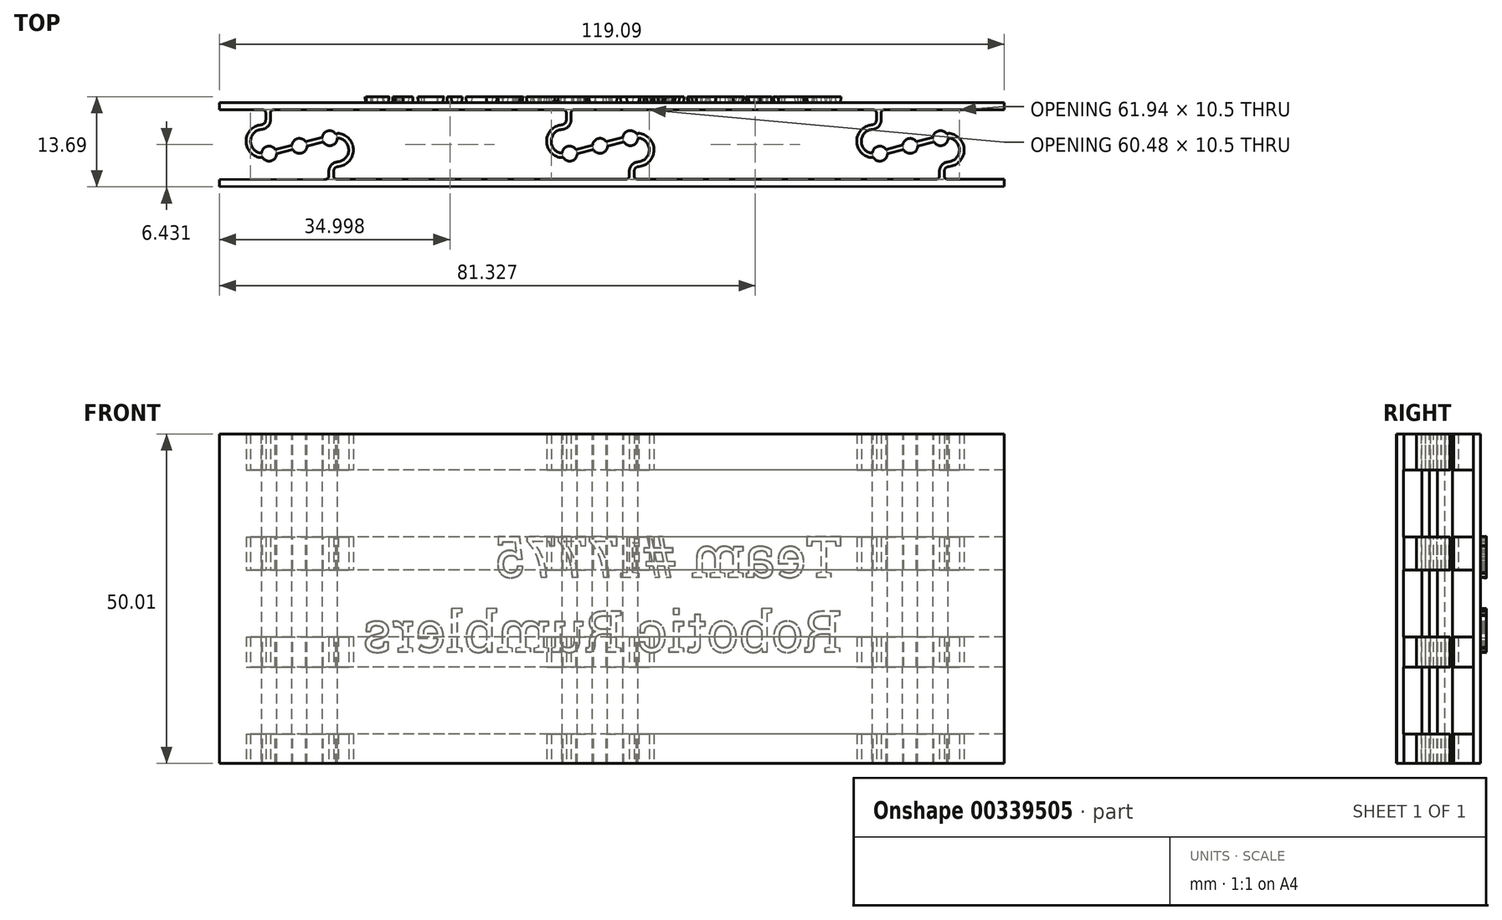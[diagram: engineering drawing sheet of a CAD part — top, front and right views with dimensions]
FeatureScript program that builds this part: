
annotation { "Feature Type Name" : "Feature", "Feature Type Description" : "" }
export const myFeature = defineFeature(function(context is Context, id is Id, definition is map)
    precondition{}
    {
        {
            var Q0;
            Q0=qCreatedBy(makeId("Top.planeOp"),FACE);
            var sketch = newSketch(context, id + "F0", { "sketchPlane" : qUnion([Q0])});
            skLineSegment(sketch, "E0", {"start": v(159.96, 0.09) * mm, "end": v(159.96, -1.43) * mm});
            skLineSegment(sketch, "E1", {"start": v(160.97, 0.09) * mm, "end": v(160.97, -1.43) * mm});
            skArc(sketch, "E2", {"start": v(160.97, -1.43) * mm, "mid": v(160.38, -2.87) * mm, "end": v(158.93, -3.46) * mm});
            skArc(sketch, "E3", {"start": v(159.96, -1.43) * mm, "mid": v(159.67, -2.16) * mm, "end": v(158.95, -2.48) * mm});
            skArc(sketch, "E4", {"start": v(158.93, -3.46) * mm, "mid": v(156.76, -5.9) * mm, "end": v(158.8, -8.45) * mm});
            skArc(sketch, "E5", {"start": v(158.95, -2.48) * mm, "mid": v(155.8, -5.9) * mm, "end": v(158.81, -9.43) * mm});
            skLineSegment(sketch, "E6", {"start": v(174.33, -13.38) * mm, "end": v(174.33, -12.37) * mm});
            skLineSegment(sketch, "E7", {"start": v(173.31, -13.38) * mm, "end": v(173.31, -12.37) * mm});
            skArc(sketch, "E8", {"start": v(173.31, -12.37) * mm, "mid": v(173.9, -10.94) * mm, "end": v(175.3, -10.32) * mm});
            skArc(sketch, "E9", {"start": v(174.33, -12.37) * mm, "mid": v(174.63, -11.63) * mm, "end": v(175.37, -11.32) * mm});
            skArc(sketch, "E10", {"start": v(175.3, -10.32) * mm, "mid": v(177.55, -7.87) * mm, "end": v(175.43, -5.3) * mm});
            skArc(sketch, "E11", {"start": v(175.37, -11.32) * mm, "mid": v(178.55, -7.83) * mm, "end": v(175.4, -4.29) * mm});
            skLineSegment(sketch, "E12", {"start": v(159.04, -9.42) * mm, "end": v(175.18, -5.32) * mm});
            skLineSegment(sketch, "E13", {"start": v(175.2, -4.3) * mm, "end": v(159.06, -8.44) * mm});
            skPoint(sketch, "E14.visualSharp", {"position": v(158.93, -8.47) * mm});
            skArc(sketch, "E14.filletArc", {"start": v(158.8, -8.45) * mm, "mid": v(158.92, -8.46) * mm, "end": v(159.06, -8.44) * mm});
            skPoint(sketch, "E15.visualSharp", {"position": v(158.93, -9.45) * mm});
            skArc(sketch, "E15.filletArc", {"start": v(158.81, -9.43) * mm, "mid": v(158.93, -9.44) * mm, "end": v(159.04, -9.42) * mm});
            skPoint(sketch, "E16.visualSharp", {"position": v(175.3, -4.28) * mm});
            skArc(sketch, "E16.filletArc", {"start": v(175.4, -4.29) * mm, "mid": v(175.3, -4.29) * mm, "end": v(175.2, -4.3) * mm});
            skPoint(sketch, "E17.visualSharp", {"position": v(175.3, -5.29) * mm});
            skArc(sketch, "E17.filletArc", {"start": v(175.43, -5.3) * mm, "mid": v(175.3, -5.3) * mm, "end": v(175.18, -5.32) * mm});
            skLineSegment(sketch, "E18", {"start": v(44.92, -13.98) * mm, "end": v(172.72, -13.98) * mm});
            skLineSegment(sketch, "E19", {"start": v(161.57, 0.68) * mm, "end": v(187.04, 0.68) * mm});
            skLineSegment(sketch, "E20", {"start": v(187.04, 0.68) * mm, "end": v(187.04, 2.22) * mm});
            skLineSegment(sketch, "E21", {"start": v(174.93, -13.98) * mm, "end": v(187.04, -13.98) * mm});
            skLineSegment(sketch, "E22", {"start": v(187.04, -13.98) * mm, "end": v(187.04, -15.5) * mm});
            skPoint(sketch, "E23.visualSharp", {"position": v(160.97, 0.68) * mm});
            skArc(sketch, "E23.filletArc", {"start": v(161.57, 0.68) * mm, "mid": v(161.15, 0.5) * mm, "end": v(160.97, 0.09) * mm});
            skPoint(sketch, "E24.visualSharp", {"position": v(159.96, 0.68) * mm});
            skArc(sketch, "E24.filletArc", {"start": v(159.96, 0.09) * mm, "mid": v(159.78, 0.5) * mm, "end": v(159.36, 0.68) * mm});
            skPoint(sketch, "E25.visualSharp", {"position": v(174.33, -13.98) * mm});
            skArc(sketch, "E25.filletArc", {"start": v(174.33, -13.38) * mm, "mid": v(174.5, -13.8) * mm, "end": v(174.93, -13.98) * mm});
            skPoint(sketch, "E26.visualSharp", {"position": v(173.31, -13.98) * mm});
            skArc(sketch, "E26.filletArc", {"start": v(172.72, -13.98) * mm, "mid": v(173.14, -13.8) * mm, "end": v(173.31, -13.38) * mm});
            skLineSegment(sketch, "E27", {"start": v(31.57, 0.09) * mm, "end": v(31.57, -1.43) * mm});
            skArc(sketch, "E28", {"start": v(31.57, -1.43) * mm, "mid": v(30.97, -2.87) * mm, "end": v(29.52, -3.46) * mm});
            skArc(sketch, "E29", {"start": v(30.55, -1.43) * mm, "mid": v(30.26, -2.16) * mm, "end": v(29.54, -2.48) * mm});
            skArc(sketch, "E30", {"start": v(29.52, -3.46) * mm, "mid": v(27.35, -5.9) * mm, "end": v(29.38, -8.45) * mm});
            skArc(sketch, "E31", {"start": v(29.54, -2.48) * mm, "mid": v(26.38, -5.9) * mm, "end": v(29.4, -9.43) * mm});
            skLineSegment(sketch, "E32", {"start": v(44.92, -13.38) * mm, "end": v(44.92, -12.37) * mm});
            skLineSegment(sketch, "E33", {"start": v(43.9, -13.38) * mm, "end": v(43.9, -12.37) * mm});
            skArc(sketch, "E34", {"start": v(43.9, -12.37) * mm, "mid": v(44.48, -10.94) * mm, "end": v(45.89, -10.32) * mm});
            skArc(sketch, "E35", {"start": v(44.92, -12.37) * mm, "mid": v(45.22, -11.63) * mm, "end": v(45.96, -11.32) * mm});
            skArc(sketch, "E36", {"start": v(45.89, -10.32) * mm, "mid": v(48.14, -7.87) * mm, "end": v(46.02, -5.3) * mm});
            skArc(sketch, "E37", {"start": v(45.96, -11.32) * mm, "mid": v(49.14, -7.83) * mm, "end": v(46, -4.29) * mm});
            skLineSegment(sketch, "E38", {"start": v(29.63, -9.42) * mm, "end": v(45.77, -5.32) * mm});
            skLineSegment(sketch, "E39", {"start": v(45.78, -4.3) * mm, "end": v(29.65, -8.44) * mm});
            skPoint(sketch, "E40.visualSharp", {"position": v(29.52, -8.47) * mm});
            skArc(sketch, "E40.filletArc", {"start": v(29.38, -8.45) * mm, "mid": v(29.52, -8.46) * mm, "end": v(29.65, -8.44) * mm});
            skPoint(sketch, "E41.visualSharp", {"position": v(29.52, -9.45) * mm});
            skArc(sketch, "E41.filletArc", {"start": v(29.4, -9.43) * mm, "mid": v(29.52, -9.44) * mm, "end": v(29.63, -9.42) * mm});
            skPoint(sketch, "E42.visualSharp", {"position": v(45.89, -4.28) * mm});
            skArc(sketch, "E42.filletArc", {"start": v(46, -4.29) * mm, "mid": v(45.9, -4.29) * mm, "end": v(45.78, -4.3) * mm});
            skPoint(sketch, "E43.visualSharp", {"position": v(45.89, -5.29) * mm});
            skArc(sketch, "E43.filletArc", {"start": v(46.02, -5.3) * mm, "mid": v(45.9, -5.3) * mm, "end": v(45.77, -5.32) * mm});
            skPoint(sketch, "E44.visualSharp", {"position": v(31.57, 0) * mm});
            skArc(sketch, "E44.filletArc", {"start": v(32.16, 0.68) * mm, "mid": v(31.74, 0.5) * mm, "end": v(31.57, 0.09) * mm});
            skPoint(sketch, "E45.visualSharp", {"position": v(44.92, -13.98) * mm});
            skArc(sketch, "E45.filletArc", {"start": v(44.92, -13.38) * mm, "mid": v(45.1, -13.8) * mm, "end": v(45.52, -13.98) * mm});
            skPoint(sketch, "E46.visualSharp", {"position": v(43.9, -13.98) * mm});
            skArc(sketch, "E46.filletArc", {"start": v(43.31, -13.98) * mm, "mid": v(43.73, -13.8) * mm, "end": v(43.9, -13.38) * mm});
            skLineSegment(sketch, "E47", {"start": v(187.04, 2.22) * mm, "end": v(20.7, 2.22) * mm});
            skLineSegment(sketch, "E48", {"start": v(43.31, -13.98) * mm, "end": v(20.7, -14.1) * mm});
            skLineSegment(sketch, "E49", {"start": v(20.7, -14.1) * mm, "end": v(20.71, -15.63) * mm});
            skLineSegment(sketch, "E50", {"start": v(20.71, -15.63) * mm, "end": v(187.04, -15.5) * mm});
            skLineSegment(sketch, "E51", {"start": v(20.7, 2.22) * mm, "end": v(20.7, 0.7) * mm});
            skLineSegment(sketch, "E52", {"start": v(30.55, -1.43) * mm, "end": v(30.55, 0.1) * mm});
            skLineSegment(sketch, "E53", {"start": v(29.95, 0.7) * mm, "end": v(20.7, 0.7) * mm});
            skPoint(sketch, "E54.visualSharp", {"position": v(30.55, 0.7) * mm});
            skArc(sketch, "E54.filletArc", {"start": v(30.55, 0.1) * mm, "mid": v(30.38, 0.52) * mm, "end": v(29.95, 0.7) * mm});
            skLineSegment(sketch, "E55", {"start": v(94.24, 0.09) * mm, "end": v(94.24, -1.43) * mm});
            skLineSegment(sketch, "E56", {"start": v(95.25, 0.09) * mm, "end": v(95.25, -1.43) * mm});
            skArc(sketch, "E57", {"start": v(95.25, -1.43) * mm, "mid": v(94.66, -2.87) * mm, "end": v(93.21, -3.46) * mm});
            skArc(sketch, "E58", {"start": v(94.24, -1.43) * mm, "mid": v(93.94, -2.16) * mm, "end": v(93.23, -2.48) * mm});
            skArc(sketch, "E59", {"start": v(93.21, -3.46) * mm, "mid": v(91.04, -5.9) * mm, "end": v(93.07, -8.45) * mm});
            skArc(sketch, "E60", {"start": v(93.23, -2.48) * mm, "mid": v(90.07, -5.9) * mm, "end": v(93.1, -9.43) * mm});
            skLineSegment(sketch, "E61", {"start": v(108.61, -13.38) * mm, "end": v(108.61, -12.37) * mm});
            skLineSegment(sketch, "E62", {"start": v(107.6, -13.38) * mm, "end": v(107.6, -12.37) * mm});
            skArc(sketch, "E63", {"start": v(107.6, -12.37) * mm, "mid": v(108.17, -10.94) * mm, "end": v(109.57, -10.32) * mm});
            skArc(sketch, "E64", {"start": v(108.61, -12.37) * mm, "mid": v(108.91, -11.63) * mm, "end": v(109.64, -11.32) * mm});
            skArc(sketch, "E65", {"start": v(109.57, -10.32) * mm, "mid": v(111.83, -7.87) * mm, "end": v(109.7, -5.3) * mm});
            skArc(sketch, "E66", {"start": v(109.64, -11.32) * mm, "mid": v(112.83, -7.83) * mm, "end": v(109.69, -4.29) * mm});
            skLineSegment(sketch, "E67", {"start": v(93.32, -9.42) * mm, "end": v(109.46, -5.32) * mm});
            skLineSegment(sketch, "E68", {"start": v(109.47, -4.3) * mm, "end": v(93.34, -8.44) * mm});
            skPoint(sketch, "E69.visualSharp", {"position": v(93.21, -8.47) * mm});
            skArc(sketch, "E69.filletArc", {"start": v(93.07, -8.45) * mm, "mid": v(93.2, -8.46) * mm, "end": v(93.34, -8.44) * mm});
            skPoint(sketch, "E70.visualSharp", {"position": v(93.21, -9.45) * mm});
            skArc(sketch, "E70.filletArc", {"start": v(93.1, -9.43) * mm, "mid": v(93.2, -9.44) * mm, "end": v(93.32, -9.42) * mm});
            skPoint(sketch, "E71.visualSharp", {"position": v(109.57, -4.28) * mm});
            skArc(sketch, "E71.filletArc", {"start": v(109.69, -4.29) * mm, "mid": v(109.58, -4.29) * mm, "end": v(109.47, -4.3) * mm});
            skPoint(sketch, "E72.visualSharp", {"position": v(109.57, -5.29) * mm});
            skArc(sketch, "E72.filletArc", {"start": v(109.7, -5.3) * mm, "mid": v(109.58, -5.3) * mm, "end": v(109.46, -5.32) * mm});
            skPoint(sketch, "E73.visualSharp", {"position": v(95.25, 0.68) * mm});
            skArc(sketch, "E73.filletArc", {"start": v(95.85, 0.68) * mm, "mid": v(95.43, 0.5) * mm, "end": v(95.25, 0.09) * mm});
            skPoint(sketch, "E74.visualSharp", {"position": v(94.24, 0.68) * mm});
            skArc(sketch, "E74.filletArc", {"start": v(94.24, 0.09) * mm, "mid": v(94.06, 0.5) * mm, "end": v(93.64, 0.68) * mm});
            skPoint(sketch, "E75.visualSharp", {"position": v(108.61, -13.98) * mm});
            skArc(sketch, "E75.filletArc", {"start": v(108.61, -13.38) * mm, "mid": v(108.79, -13.8) * mm, "end": v(109.2, -13.98) * mm});
            skPoint(sketch, "E76.visualSharp", {"position": v(107.6, -13.98) * mm});
            skArc(sketch, "E76.filletArc", {"start": v(107, -13.98) * mm, "mid": v(107.42, -13.8) * mm, "end": v(107.6, -13.38) * mm});
            skLineSegment(sketch, "E77", {"start": v(32.16, 0.68) * mm, "end": v(93.64, 0.68) * mm});
            skLineSegment(sketch, "E78", {"start": v(95.85, 0.68) * mm, "end": v(159.36, 0.68) * mm});
            skSolve(sketch);
        }
        {
            var Q0;
            Q0=makeQuery(id+"F0.imprint","IMPRINT",FACE,{"disambiguationData":[TD([[makeQuery(id+"F0.imprint","IMPRINT",EDGE,{"derivedFrom":sQuery(id+"F0.wireOp",EDGE,"E0")}),1.0]])]});
            extrude(context, id + "F1", {"entities" : qUnion([Q0]), "depth" : 69.85 * mm});
        }
        {
            var Q0;
            Q0=makeQuery(id+"F1.opExtrude","SWEPT_FACE",FACE,{"disambiguationData":[OSD([sQuery(id+"F0.wireOp",EDGE,"E51")])]});
            var sketch = newSketch(context, id + "F2", { "sketchPlane" : qUnion([Q0])});
            skLineSegment(sketch, "E79.bottom", {"start": v(-0.7, 6.25) * mm, "end": v(14.06, 6.25) * mm});
            skLineSegment(sketch, "E79.top", {"start": v(-0.7, 20.44) * mm, "end": v(14.06, 20.44) * mm});
            skLineSegment(sketch, "E79.left", {"start": v(-0.7, 6.25) * mm, "end": v(-0.7, 20.44) * mm});
            skLineSegment(sketch, "E79.right", {"start": v(14.06, 6.25) * mm, "end": v(14.06, 20.44) * mm});
            skLineSegment(sketch, "E80.bottom", {"start": v(-0.7, 26.84) * mm, "end": v(14.06, 26.84) * mm});
            skLineSegment(sketch, "E80.top", {"start": v(-0.7, 41.03) * mm, "end": v(14.06, 41.03) * mm});
            skLineSegment(sketch, "E80.left", {"start": v(-0.7, 26.84) * mm, "end": v(-0.7, 41.03) * mm});
            skLineSegment(sketch, "E80.right", {"start": v(14.06, 26.84) * mm, "end": v(14.06, 41.03) * mm});
            skLineSegment(sketch, "E81.bottom", {"start": v(-0.7, 48.02) * mm, "end": v(14.06, 48.02) * mm});
            skLineSegment(sketch, "E81.top", {"start": v(-0.7, 62.2) * mm, "end": v(14.06, 62.2) * mm});
            skLineSegment(sketch, "E81.left", {"start": v(-0.7, 48.02) * mm, "end": v(-0.7, 62.2) * mm});
            skLineSegment(sketch, "E81.right", {"start": v(14.06, 48.02) * mm, "end": v(14.06, 62.2) * mm});
            skSolve(sketch);
        }
        {
            var Q0;
            Q0=makeQuery(id+"F2.imprint","IMPRINT",FACE,{"disambiguationData":[TD([[makeQuery(id+"F2.imprint","IMPRINT",EDGE,{"derivedFrom":sQuery(id+"F2.wireOp",EDGE,"E79.bottom")}),1.0]])]});
            var Q1;
            Q1=makeQuery(id+"F2.imprint","IMPRINT",FACE,{"disambiguationData":[TD([[makeQuery(id+"F2.imprint","IMPRINT",EDGE,{"derivedFrom":sQuery(id+"F2.wireOp",EDGE,"E80.bottom")}),1.0]])]});
            var Q2;
            Q2=makeQuery(id+"F2.imprint","IMPRINT",FACE,{"disambiguationData":[TD([[makeQuery(id+"F2.imprint","IMPRINT",EDGE,{"derivedFrom":sQuery(id+"F2.wireOp",EDGE,"E81.bottom")}),1.0]])]});
            extrude(context, id + "F3", {"entities" : qUnion([Q0, Q1, Q2]), "operationType" : NewBodyOperationType.REMOVE, "oppositeDirection" : true, "depth" : 254 * mm});
        }
        {
            var Q0;
            Q0=makeQuery(id+"F1.opExtrude","SWEPT_FACE",FACE,{"disambiguationData":[OSD([sQuery(id+"F0.wireOp",EDGE,"E47")])]});
            var sketch = newSketch(context, id + "F4", { "sketchPlane" : qUnion([Q0])});
            skText(sketch, "E82", { "text": "Team #17775\nRobotic Rumblers", "fontName": "RobotoSlab-Regular.ttf"});
            const initialGuessF4  = {"E82": [-0.15258, 0.03953, 1, 0, 0.00865]};
            skSetInitialGuess(sketch, initialGuessF4);
            skSolve(sketch);
        }
        {
            var Q0;
            Q0=qSketchRegion(id+"F4",true);
            extrude(context, id + "F5", {"entities" : qUnion([Q0]), "operationType" : NewBodyOperationType.ADD, "depth" : 1.27 * mm, "hasDraft" : true, "draftAngle" : 3 * degree});
        }
        {
            var Q0;
            Q0=makeQuery(id+"F1.opExtrude","SWEPT_BODY",BODY,{"disambiguationData":[OSD([sQuery(id+"F0.wireOp",EDGE,"E0"),sQuery(id+"F0.wireOp",EDGE,"E1"),sQuery(id+"F0.wireOp",EDGE,"E2"),sQuery(id+"F0.wireOp",EDGE,"E3"),sQuery(id+"F0.wireOp",EDGE,"E4"),sQuery(id+"F0.wireOp",EDGE,"E5"),sQuery(id+"F0.wireOp",EDGE,"E6"),sQuery(id+"F0.wireOp",EDGE,"E7"),sQuery(id+"F0.wireOp",EDGE,"E8"),sQuery(id+"F0.wireOp",EDGE,"E9"),sQuery(id+"F0.wireOp",EDGE,"E10"),sQuery(id+"F0.wireOp",EDGE,"E11"),sQuery(id+"F0.wireOp",EDGE,"E12"),sQuery(id+"F0.wireOp",EDGE,"E13"),sQuery(id+"F0.wireOp",EDGE,"E14.filletArc"),sQuery(id+"F0.wireOp",EDGE,"E15.filletArc"),sQuery(id+"F0.wireOp",EDGE,"E16.filletArc"),sQuery(id+"F0.wireOp",EDGE,"E17.filletArc"),sQuery(id+"F0.wireOp",EDGE,"E18"),sQuery(id+"F0.wireOp",EDGE,"E19"),sQuery(id+"F0.wireOp",EDGE,"E20"),sQuery(id+"F0.wireOp",EDGE,"E21"),sQuery(id+"F0.wireOp",EDGE,"E22"),sQuery(id+"F0.wireOp",EDGE,"E23.filletArc"),sQuery(id+"F0.wireOp",EDGE,"E24.filletArc"),sQuery(id+"F0.wireOp",EDGE,"E25.filletArc"),sQuery(id+"F0.wireOp",EDGE,"E26.filletArc"),sQuery(id+"F0.wireOp",EDGE,"E27"),sQuery(id+"F0.wireOp",EDGE,"E28"),sQuery(id+"F0.wireOp",EDGE,"E29"),sQuery(id+"F0.wireOp",EDGE,"E30"),sQuery(id+"F0.wireOp",EDGE,"E31"),sQuery(id+"F0.wireOp",EDGE,"E32"),sQuery(id+"F0.wireOp",EDGE,"E33"),sQuery(id+"F0.wireOp",EDGE,"E34"),sQuery(id+"F0.wireOp",EDGE,"E35"),sQuery(id+"F0.wireOp",EDGE,"E36"),sQuery(id+"F0.wireOp",EDGE,"E37"),sQuery(id+"F0.wireOp",EDGE,"E38"),sQuery(id+"F0.wireOp",EDGE,"E39"),sQuery(id+"F0.wireOp",EDGE,"E40.filletArc"),sQuery(id+"F0.wireOp",EDGE,"E41.filletArc"),sQuery(id+"F0.wireOp",EDGE,"E42.filletArc"),sQuery(id+"F0.wireOp",EDGE,"E43.filletArc"),sQuery(id+"F0.wireOp",EDGE,"E44.filletArc"),sQuery(id+"F0.wireOp",EDGE,"E45.filletArc"),sQuery(id+"F0.wireOp",EDGE,"E46.filletArc"),sQuery(id+"F0.wireOp",EDGE,"E47"),sQuery(id+"F0.wireOp",EDGE,"E48"),sQuery(id+"F0.wireOp",EDGE,"E49"),sQuery(id+"F0.wireOp",EDGE,"E50"),sQuery(id+"F0.wireOp",EDGE,"E51"),sQuery(id+"F0.wireOp",EDGE,"E52"),sQuery(id+"F0.wireOp",EDGE,"E53"),sQuery(id+"F0.wireOp",EDGE,"E54.filletArc"),sQuery(id+"F0.wireOp",EDGE,"E55"),sQuery(id+"F0.wireOp",EDGE,"E56"),sQuery(id+"F0.wireOp",EDGE,"E57"),sQuery(id+"F0.wireOp",EDGE,"E58"),sQuery(id+"F0.wireOp",EDGE,"E59"),sQuery(id+"F0.wireOp",EDGE,"E60"),sQuery(id+"F0.wireOp",EDGE,"E61"),sQuery(id+"F0.wireOp",EDGE,"E62"),sQuery(id+"F0.wireOp",EDGE,"E63"),sQuery(id+"F0.wireOp",EDGE,"E64"),sQuery(id+"F0.wireOp",EDGE,"E65"),sQuery(id+"F0.wireOp",EDGE,"E66"),sQuery(id+"F0.wireOp",EDGE,"E67"),sQuery(id+"F0.wireOp",EDGE,"E68"),sQuery(id+"F0.wireOp",EDGE,"E69.filletArc"),sQuery(id+"F0.wireOp",EDGE,"E70.filletArc"),sQuery(id+"F0.wireOp",EDGE,"E71.filletArc"),sQuery(id+"F0.wireOp",EDGE,"E72.filletArc"),sQuery(id+"F0.wireOp",EDGE,"E73.filletArc"),sQuery(id+"F0.wireOp",EDGE,"E74.filletArc"),sQuery(id+"F0.wireOp",EDGE,"E75.filletArc"),sQuery(id+"F0.wireOp",EDGE,"E76.filletArc"),sQuery(id+"F0.wireOp",EDGE,"E77"),sQuery(id+"F0.wireOp",EDGE,"E78")])]});
            transform(context, id + "F6", {"entities" : qUnion([Q0]), "transformType" : TransformType.TRANSLATION_3D, "dx" : -104.65 * mm, "dy" : 0 * mm, "dz" : 0 * mm, "makeCopy" : false});
        }
        {
            var Q0;
            Q0=makeQuery(id+"F1.opExtrude","SWEPT_BODY",BODY,{"disambiguationData":[OSD([sQuery(id+"F0.wireOp",EDGE,"E0"),sQuery(id+"F0.wireOp",EDGE,"E1"),sQuery(id+"F0.wireOp",EDGE,"E2"),sQuery(id+"F0.wireOp",EDGE,"E3"),sQuery(id+"F0.wireOp",EDGE,"E4"),sQuery(id+"F0.wireOp",EDGE,"E5"),sQuery(id+"F0.wireOp",EDGE,"E6"),sQuery(id+"F0.wireOp",EDGE,"E7"),sQuery(id+"F0.wireOp",EDGE,"E8"),sQuery(id+"F0.wireOp",EDGE,"E9"),sQuery(id+"F0.wireOp",EDGE,"E10"),sQuery(id+"F0.wireOp",EDGE,"E11"),sQuery(id+"F0.wireOp",EDGE,"E12"),sQuery(id+"F0.wireOp",EDGE,"E13"),sQuery(id+"F0.wireOp",EDGE,"E14.filletArc"),sQuery(id+"F0.wireOp",EDGE,"E15.filletArc"),sQuery(id+"F0.wireOp",EDGE,"E16.filletArc"),sQuery(id+"F0.wireOp",EDGE,"E17.filletArc"),sQuery(id+"F0.wireOp",EDGE,"E18"),sQuery(id+"F0.wireOp",EDGE,"E19"),sQuery(id+"F0.wireOp",EDGE,"E20"),sQuery(id+"F0.wireOp",EDGE,"E21"),sQuery(id+"F0.wireOp",EDGE,"E22"),sQuery(id+"F0.wireOp",EDGE,"E23.filletArc"),sQuery(id+"F0.wireOp",EDGE,"E24.filletArc"),sQuery(id+"F0.wireOp",EDGE,"E25.filletArc"),sQuery(id+"F0.wireOp",EDGE,"E26.filletArc"),sQuery(id+"F0.wireOp",EDGE,"E27"),sQuery(id+"F0.wireOp",EDGE,"E28"),sQuery(id+"F0.wireOp",EDGE,"E29"),sQuery(id+"F0.wireOp",EDGE,"E30"),sQuery(id+"F0.wireOp",EDGE,"E31"),sQuery(id+"F0.wireOp",EDGE,"E32"),sQuery(id+"F0.wireOp",EDGE,"E33"),sQuery(id+"F0.wireOp",EDGE,"E34"),sQuery(id+"F0.wireOp",EDGE,"E35"),sQuery(id+"F0.wireOp",EDGE,"E36"),sQuery(id+"F0.wireOp",EDGE,"E37"),sQuery(id+"F0.wireOp",EDGE,"E38"),sQuery(id+"F0.wireOp",EDGE,"E39"),sQuery(id+"F0.wireOp",EDGE,"E40.filletArc"),sQuery(id+"F0.wireOp",EDGE,"E41.filletArc"),sQuery(id+"F0.wireOp",EDGE,"E42.filletArc"),sQuery(id+"F0.wireOp",EDGE,"E43.filletArc"),sQuery(id+"F0.wireOp",EDGE,"E44.filletArc"),sQuery(id+"F0.wireOp",EDGE,"E45.filletArc"),sQuery(id+"F0.wireOp",EDGE,"E46.filletArc"),sQuery(id+"F0.wireOp",EDGE,"E47"),sQuery(id+"F0.wireOp",EDGE,"E48"),sQuery(id+"F0.wireOp",EDGE,"E49"),sQuery(id+"F0.wireOp",EDGE,"E50"),sQuery(id+"F0.wireOp",EDGE,"E51"),sQuery(id+"F0.wireOp",EDGE,"E52"),sQuery(id+"F0.wireOp",EDGE,"E53"),sQuery(id+"F0.wireOp",EDGE,"E54.filletArc"),sQuery(id+"F0.wireOp",EDGE,"E55"),sQuery(id+"F0.wireOp",EDGE,"E56"),sQuery(id+"F0.wireOp",EDGE,"E57"),sQuery(id+"F0.wireOp",EDGE,"E58"),sQuery(id+"F0.wireOp",EDGE,"E59"),sQuery(id+"F0.wireOp",EDGE,"E60"),sQuery(id+"F0.wireOp",EDGE,"E61"),sQuery(id+"F0.wireOp",EDGE,"E62"),sQuery(id+"F0.wireOp",EDGE,"E63"),sQuery(id+"F0.wireOp",EDGE,"E64"),sQuery(id+"F0.wireOp",EDGE,"E65"),sQuery(id+"F0.wireOp",EDGE,"E66"),sQuery(id+"F0.wireOp",EDGE,"E67"),sQuery(id+"F0.wireOp",EDGE,"E68"),sQuery(id+"F0.wireOp",EDGE,"E69.filletArc"),sQuery(id+"F0.wireOp",EDGE,"E70.filletArc"),sQuery(id+"F0.wireOp",EDGE,"E71.filletArc"),sQuery(id+"F0.wireOp",EDGE,"E72.filletArc"),sQuery(id+"F0.wireOp",EDGE,"E73.filletArc"),sQuery(id+"F0.wireOp",EDGE,"E74.filletArc"),sQuery(id+"F0.wireOp",EDGE,"E75.filletArc"),sQuery(id+"F0.wireOp",EDGE,"E76.filletArc"),sQuery(id+"F0.wireOp",EDGE,"E77"),sQuery(id+"F0.wireOp",EDGE,"E78")])]});
            var Q1;
            Q1=qCreatedBy(makeId("Origin.pointOp"),VERTEX);
            transform(context, id + "F7", {"entities" : qUnion([Q0]), "transformType" : TransformType.SCALE_UNIFORMLY, "scale" : .716, "scalePoint" : qUnion([Q1]), "makeCopy" : false});
        }
        {
            var Q0;
            Q0=makeQuery(id+"F1.opExtrude","CAP_FACE",FACE,{"disambiguationData":[OSD([sQuery(id+"F0.wireOp",EDGE,"E0"),sQuery(id+"F0.wireOp",EDGE,"E1"),sQuery(id+"F0.wireOp",EDGE,"E2"),sQuery(id+"F0.wireOp",EDGE,"E3"),sQuery(id+"F0.wireOp",EDGE,"E4"),sQuery(id+"F0.wireOp",EDGE,"E5"),sQuery(id+"F0.wireOp",EDGE,"E6"),sQuery(id+"F0.wireOp",EDGE,"E7"),sQuery(id+"F0.wireOp",EDGE,"E8"),sQuery(id+"F0.wireOp",EDGE,"E9"),sQuery(id+"F0.wireOp",EDGE,"E10"),sQuery(id+"F0.wireOp",EDGE,"E11"),sQuery(id+"F0.wireOp",EDGE,"E12"),sQuery(id+"F0.wireOp",EDGE,"E13"),sQuery(id+"F0.wireOp",EDGE,"E14.filletArc"),sQuery(id+"F0.wireOp",EDGE,"E15.filletArc"),sQuery(id+"F0.wireOp",EDGE,"E16.filletArc"),sQuery(id+"F0.wireOp",EDGE,"E17.filletArc"),sQuery(id+"F0.wireOp",EDGE,"E18"),sQuery(id+"F0.wireOp",EDGE,"E19"),sQuery(id+"F0.wireOp",EDGE,"E20"),sQuery(id+"F0.wireOp",EDGE,"E21"),sQuery(id+"F0.wireOp",EDGE,"E22"),sQuery(id+"F0.wireOp",EDGE,"E23.filletArc"),sQuery(id+"F0.wireOp",EDGE,"E24.filletArc"),sQuery(id+"F0.wireOp",EDGE,"E25.filletArc"),sQuery(id+"F0.wireOp",EDGE,"E26.filletArc"),sQuery(id+"F0.wireOp",EDGE,"E27"),sQuery(id+"F0.wireOp",EDGE,"E28"),sQuery(id+"F0.wireOp",EDGE,"E29"),sQuery(id+"F0.wireOp",EDGE,"E30"),sQuery(id+"F0.wireOp",EDGE,"E31"),sQuery(id+"F0.wireOp",EDGE,"E32"),sQuery(id+"F0.wireOp",EDGE,"E33"),sQuery(id+"F0.wireOp",EDGE,"E34"),sQuery(id+"F0.wireOp",EDGE,"E35"),sQuery(id+"F0.wireOp",EDGE,"E36"),sQuery(id+"F0.wireOp",EDGE,"E37"),sQuery(id+"F0.wireOp",EDGE,"E38"),sQuery(id+"F0.wireOp",EDGE,"E39"),sQuery(id+"F0.wireOp",EDGE,"E40.filletArc"),sQuery(id+"F0.wireOp",EDGE,"E41.filletArc"),sQuery(id+"F0.wireOp",EDGE,"E42.filletArc"),sQuery(id+"F0.wireOp",EDGE,"E43.filletArc"),sQuery(id+"F0.wireOp",EDGE,"E44.filletArc"),sQuery(id+"F0.wireOp",EDGE,"E45.filletArc"),sQuery(id+"F0.wireOp",EDGE,"E46.filletArc"),sQuery(id+"F0.wireOp",EDGE,"E47"),sQuery(id+"F0.wireOp",EDGE,"E48"),sQuery(id+"F0.wireOp",EDGE,"E49"),sQuery(id+"F0.wireOp",EDGE,"E50"),sQuery(id+"F0.wireOp",EDGE,"E51"),sQuery(id+"F0.wireOp",EDGE,"E52"),sQuery(id+"F0.wireOp",EDGE,"E53"),sQuery(id+"F0.wireOp",EDGE,"E54.filletArc"),sQuery(id+"F0.wireOp",EDGE,"E55"),sQuery(id+"F0.wireOp",EDGE,"E56"),sQuery(id+"F0.wireOp",EDGE,"E57"),sQuery(id+"F0.wireOp",EDGE,"E58"),sQuery(id+"F0.wireOp",EDGE,"E59"),sQuery(id+"F0.wireOp",EDGE,"E60"),sQuery(id+"F0.wireOp",EDGE,"E61"),sQuery(id+"F0.wireOp",EDGE,"E62"),sQuery(id+"F0.wireOp",EDGE,"E63"),sQuery(id+"F0.wireOp",EDGE,"E64"),sQuery(id+"F0.wireOp",EDGE,"E65"),sQuery(id+"F0.wireOp",EDGE,"E66"),sQuery(id+"F0.wireOp",EDGE,"E67"),sQuery(id+"F0.wireOp",EDGE,"E68"),sQuery(id+"F0.wireOp",EDGE,"E69.filletArc"),sQuery(id+"F0.wireOp",EDGE,"E70.filletArc"),sQuery(id+"F0.wireOp",EDGE,"E71.filletArc"),sQuery(id+"F0.wireOp",EDGE,"E72.filletArc"),sQuery(id+"F0.wireOp",EDGE,"E73.filletArc"),sQuery(id+"F0.wireOp",EDGE,"E74.filletArc"),sQuery(id+"F0.wireOp",EDGE,"E75.filletArc"),sQuery(id+"F0.wireOp",EDGE,"E76.filletArc"),sQuery(id+"F0.wireOp",EDGE,"E77"),sQuery(id+"F0.wireOp",EDGE,"E78")])],"isStart":false});
            var sketch = newSketch(context, id + "F8", { "sketchPlane" : qUnion([Q0])});
            skCircle(sketch, "E83", {"center": v(-47.93, -4.98) * mm, "radius": 1.14 * mm});
            skPoint(sketch, "E83.centerSnap0", {"position": v(-47.93, -5.28) * mm});
            skLineSegment(sketch, "E84", {"start": v(-47.93, -4.98) * mm, "end": v(-42, -3.47) * mm, "construction": true});
            skLineSegment(sketch, "E85", {"start": v(-47.93, -4.98) * mm, "end": v(-53.65, -6.44) * mm, "construction": true});
            skCircle(sketch, "E86", {"center": v(-52.54, -6.16) * mm, "radius": 1.14 * mm});
            skCircle(sketch, "E87", {"center": v(-43.34, -3.8) * mm, "radius": 1.14 * mm});
            skCircle(sketch, "E88", {"center": v(-2.33, -4.97) * mm, "radius": 1.14 * mm});
            skCircle(sketch, "E89", {"center": v(-6.94, -6.15) * mm, "radius": 1.14 * mm});
            skCircle(sketch, "E90", {"center": v(2.27, -3.8) * mm, "radius": 1.14 * mm});
            skCircle(sketch, "E91", {"center": v(44.73, -4.98) * mm, "radius": 1.14 * mm});
            skCircle(sketch, "E92", {"center": v(40.13, -6.16) * mm, "radius": 1.14 * mm});
            skCircle(sketch, "E93", {"center": v(49.33, -3.8) * mm, "radius": 1.14 * mm});
            skSolve(sketch);
        }
        {
            var Q0;
            {var subQ0=sQuery(id+"F8.wireOp",EDGE,"E86");var subQ1=makeQuery(id+"F1.opExtrude","CAP_EDGE",EDGE,{"disambiguationData":[OSD([sQuery(id+"F0.wireOp",EDGE,"E39")])],"isStart":false});var subQ2=makeQuery(id+"F8.imprint","INTERSECT",VERTEX,{"disambiguationData":[OD(0.0)],"derivedFrom":[subQ1,subQ0]});Q0=makeQuery(id+"F8.imprint","IMPRINT",FACE,{"disambiguationData":[TD([[makeQuery(id+"F8.imprint","IMPRINT",EDGE,{"disambiguationData":[TD([[subQ2,1.0]])],"derivedFrom":subQ0}),1.0]])]});}
            var Q1;
            {var subQ0=sQuery(id+"F8.wireOp",EDGE,"E86");var subQ1=makeQuery(id+"F1.opExtrude","CAP_EDGE",EDGE,{"disambiguationData":[OSD([sQuery(id+"F0.wireOp",EDGE,"E38")])],"isStart":false});var subQ2=makeQuery(id+"F8.imprint","INTERSECT",VERTEX,{"disambiguationData":[OD(0.0)],"derivedFrom":[subQ1,subQ0]});Q1=makeQuery(id+"F8.imprint","IMPRINT",FACE,{"disambiguationData":[TD([[makeQuery(id+"F8.imprint","IMPRINT",EDGE,{"disambiguationData":[TD([[subQ2,1.0]])],"derivedFrom":subQ0}),1.0]])]});}
            var Q2;
            {var subQ0=sQuery(id+"F8.wireOp",EDGE,"E86");var subQ1=makeQuery(id+"F1.opExtrude","CAP_EDGE",EDGE,{"disambiguationData":[OSD([sQuery(id+"F0.wireOp",EDGE,"E38")])],"isStart":false});var subQ2=makeQuery(id+"F8.imprint","INTERSECT",VERTEX,{"disambiguationData":[OD(0.0)],"derivedFrom":[subQ1,subQ0]});Q2=makeQuery(id+"F8.imprint","IMPRINT",FACE,{"disambiguationData":[TD([[makeQuery(id+"F8.imprint","IMPRINT",EDGE,{"disambiguationData":[TD([[subQ2,-1.0]])],"derivedFrom":subQ0}),1.0]])]});}
            var Q3;
            {var subQ0=sQuery(id+"F8.wireOp",EDGE,"E83");var subQ1=makeQuery(id+"F1.opExtrude","CAP_EDGE",EDGE,{"disambiguationData":[OSD([sQuery(id+"F0.wireOp",EDGE,"E39")])],"isStart":false});var subQ2=makeQuery(id+"F8.imprint","INTERSECT",VERTEX,{"disambiguationData":[OD(0.0)],"derivedFrom":[subQ1,subQ0]});Q3=makeQuery(id+"F8.imprint","IMPRINT",FACE,{"disambiguationData":[TD([[makeQuery(id+"F8.imprint","IMPRINT",EDGE,{"disambiguationData":[TD([[subQ2,1.0]])],"derivedFrom":subQ0}),1.0]])]});}
            var Q4;
            {var subQ0=sQuery(id+"F8.wireOp",EDGE,"E83");var subQ1=makeQuery(id+"F1.opExtrude","CAP_EDGE",EDGE,{"disambiguationData":[OSD([sQuery(id+"F0.wireOp",EDGE,"E38")])],"isStart":false});var subQ2=makeQuery(id+"F8.imprint","INTERSECT",VERTEX,{"disambiguationData":[OD(0.0)],"derivedFrom":[subQ1,subQ0]});Q4=makeQuery(id+"F8.imprint","IMPRINT",FACE,{"disambiguationData":[TD([[makeQuery(id+"F8.imprint","IMPRINT",EDGE,{"disambiguationData":[TD([[subQ2,1.0]])],"derivedFrom":subQ0}),1.0]])]});}
            var Q5;
            {var subQ0=sQuery(id+"F8.wireOp",EDGE,"E83");var subQ1=makeQuery(id+"F1.opExtrude","CAP_EDGE",EDGE,{"disambiguationData":[OSD([sQuery(id+"F0.wireOp",EDGE,"E38")])],"isStart":false});var subQ2=makeQuery(id+"F8.imprint","INTERSECT",VERTEX,{"disambiguationData":[OD(0.0)],"derivedFrom":[subQ1,subQ0]});Q5=makeQuery(id+"F8.imprint","IMPRINT",FACE,{"disambiguationData":[TD([[makeQuery(id+"F8.imprint","IMPRINT",EDGE,{"disambiguationData":[TD([[subQ2,-1.0]])],"derivedFrom":subQ0}),1.0]])]});}
            var Q6;
            {var subQ0=sQuery(id+"F8.wireOp",EDGE,"E87");var subQ1=makeQuery(id+"F1.opExtrude","CAP_EDGE",EDGE,{"disambiguationData":[OSD([sQuery(id+"F0.wireOp",EDGE,"E39")])],"isStart":false});var subQ2=makeQuery(id+"F8.imprint","INTERSECT",VERTEX,{"disambiguationData":[OD(0.0)],"derivedFrom":[subQ1,subQ0]});Q6=makeQuery(id+"F8.imprint","IMPRINT",FACE,{"disambiguationData":[TD([[makeQuery(id+"F8.imprint","IMPRINT",EDGE,{"disambiguationData":[TD([[subQ2,1.0]])],"derivedFrom":subQ0}),1.0]])]});}
            var Q7;
            {var subQ0=sQuery(id+"F8.wireOp",EDGE,"E87");var subQ1=makeQuery(id+"F1.opExtrude","CAP_EDGE",EDGE,{"disambiguationData":[OSD([sQuery(id+"F0.wireOp",EDGE,"E38")])],"isStart":false});var subQ2=makeQuery(id+"F8.imprint","INTERSECT",VERTEX,{"disambiguationData":[OD(0.0)],"derivedFrom":[subQ1,subQ0]});Q7=makeQuery(id+"F8.imprint","IMPRINT",FACE,{"disambiguationData":[TD([[makeQuery(id+"F8.imprint","IMPRINT",EDGE,{"disambiguationData":[TD([[subQ2,1.0]])],"derivedFrom":subQ0}),1.0]])]});}
            var Q8;
            {var subQ0=sQuery(id+"F8.wireOp",EDGE,"E87");var subQ1=makeQuery(id+"F1.opExtrude","CAP_EDGE",EDGE,{"disambiguationData":[OSD([sQuery(id+"F0.wireOp",EDGE,"E38")])],"isStart":false});var subQ2=makeQuery(id+"F8.imprint","INTERSECT",VERTEX,{"disambiguationData":[OD(0.0)],"derivedFrom":[subQ1,subQ0]});Q8=makeQuery(id+"F8.imprint","IMPRINT",FACE,{"disambiguationData":[TD([[makeQuery(id+"F8.imprint","IMPRINT",EDGE,{"disambiguationData":[TD([[subQ2,-1.0]])],"derivedFrom":subQ0}),1.0]])]});}
            var Q9;
            {var subQ0=sQuery(id+"F8.wireOp",EDGE,"E89");var subQ1=makeQuery(id+"F1.opExtrude","CAP_EDGE",EDGE,{"disambiguationData":[OSD([sQuery(id+"F0.wireOp",EDGE,"E68")])],"isStart":false});var subQ2=makeQuery(id+"F8.imprint","INTERSECT",VERTEX,{"disambiguationData":[OD(0.0)],"derivedFrom":[subQ1,subQ0]});Q9=makeQuery(id+"F8.imprint","IMPRINT",FACE,{"disambiguationData":[TD([[makeQuery(id+"F8.imprint","IMPRINT",EDGE,{"disambiguationData":[TD([[subQ2,1.0]])],"derivedFrom":subQ0}),1.0]])]});}
            var Q10;
            {var subQ0=sQuery(id+"F8.wireOp",EDGE,"E89");var subQ1=makeQuery(id+"F1.opExtrude","CAP_EDGE",EDGE,{"disambiguationData":[OSD([sQuery(id+"F0.wireOp",EDGE,"E68")])],"isStart":false});var subQ2=makeQuery(id+"F8.imprint","INTERSECT",VERTEX,{"disambiguationData":[OD(0.0)],"derivedFrom":[subQ1,subQ0]});Q10=makeQuery(id+"F8.imprint","IMPRINT",FACE,{"disambiguationData":[TD([[makeQuery(id+"F8.imprint","IMPRINT",EDGE,{"disambiguationData":[TD([[subQ2,-1.0]])],"derivedFrom":subQ0}),1.0]])]});}
            var Q11;
            {var subQ0=sQuery(id+"F8.wireOp",EDGE,"E89");var subQ1=makeQuery(id+"F1.opExtrude","CAP_EDGE",EDGE,{"disambiguationData":[OSD([sQuery(id+"F0.wireOp",EDGE,"E67")])],"isStart":false});var subQ2=makeQuery(id+"F8.imprint","INTERSECT",VERTEX,{"disambiguationData":[OD(0.0)],"derivedFrom":[subQ1,subQ0]});Q11=makeQuery(id+"F8.imprint","IMPRINT",FACE,{"disambiguationData":[TD([[makeQuery(id+"F8.imprint","IMPRINT",EDGE,{"disambiguationData":[TD([[subQ2,-1.0]])],"derivedFrom":subQ0}),1.0]])]});}
            var Q12;
            {var subQ0=sQuery(id+"F8.wireOp",EDGE,"E88");var subQ1=makeQuery(id+"F1.opExtrude","CAP_EDGE",EDGE,{"disambiguationData":[OSD([sQuery(id+"F0.wireOp",EDGE,"E68")])],"isStart":false});var subQ2=makeQuery(id+"F8.imprint","INTERSECT",VERTEX,{"disambiguationData":[OD(0.0)],"derivedFrom":[subQ1,subQ0]});Q12=makeQuery(id+"F8.imprint","IMPRINT",FACE,{"disambiguationData":[TD([[makeQuery(id+"F8.imprint","IMPRINT",EDGE,{"disambiguationData":[TD([[subQ2,1.0]])],"derivedFrom":subQ0}),1.0]])]});}
            var Q13;
            {var subQ0=sQuery(id+"F8.wireOp",EDGE,"E88");var subQ1=makeQuery(id+"F1.opExtrude","CAP_EDGE",EDGE,{"disambiguationData":[OSD([sQuery(id+"F0.wireOp",EDGE,"E68")])],"isStart":false});var subQ2=makeQuery(id+"F8.imprint","INTERSECT",VERTEX,{"disambiguationData":[OD(0.0)],"derivedFrom":[subQ1,subQ0]});Q13=makeQuery(id+"F8.imprint","IMPRINT",FACE,{"disambiguationData":[TD([[makeQuery(id+"F8.imprint","IMPRINT",EDGE,{"disambiguationData":[TD([[subQ2,-1.0]])],"derivedFrom":subQ0}),1.0]])]});}
            var Q14;
            {var subQ0=sQuery(id+"F8.wireOp",EDGE,"E88");var subQ1=makeQuery(id+"F1.opExtrude","CAP_EDGE",EDGE,{"disambiguationData":[OSD([sQuery(id+"F0.wireOp",EDGE,"E67")])],"isStart":false});var subQ2=makeQuery(id+"F8.imprint","INTERSECT",VERTEX,{"disambiguationData":[OD(0.0)],"derivedFrom":[subQ1,subQ0]});Q14=makeQuery(id+"F8.imprint","IMPRINT",FACE,{"disambiguationData":[TD([[makeQuery(id+"F8.imprint","IMPRINT",EDGE,{"disambiguationData":[TD([[subQ2,-1.0]])],"derivedFrom":subQ0}),1.0]])]});}
            var Q15;
            {var subQ0=sQuery(id+"F8.wireOp",EDGE,"E90");var subQ1=makeQuery(id+"F1.opExtrude","CAP_EDGE",EDGE,{"disambiguationData":[OSD([sQuery(id+"F0.wireOp",EDGE,"E68")])],"isStart":false});var subQ2=makeQuery(id+"F8.imprint","INTERSECT",VERTEX,{"disambiguationData":[OD(0.0)],"derivedFrom":[subQ1,subQ0]});Q15=makeQuery(id+"F8.imprint","IMPRINT",FACE,{"disambiguationData":[TD([[makeQuery(id+"F8.imprint","IMPRINT",EDGE,{"disambiguationData":[TD([[subQ2,1.0]])],"derivedFrom":subQ0}),1.0]])]});}
            var Q16;
            {var subQ0=sQuery(id+"F8.wireOp",EDGE,"E90");var subQ1=makeQuery(id+"F1.opExtrude","CAP_EDGE",EDGE,{"disambiguationData":[OSD([sQuery(id+"F0.wireOp",EDGE,"E68")])],"isStart":false});var subQ2=makeQuery(id+"F8.imprint","INTERSECT",VERTEX,{"disambiguationData":[OD(0.0)],"derivedFrom":[subQ1,subQ0]});Q16=makeQuery(id+"F8.imprint","IMPRINT",FACE,{"disambiguationData":[TD([[makeQuery(id+"F8.imprint","IMPRINT",EDGE,{"disambiguationData":[TD([[subQ2,-1.0]])],"derivedFrom":subQ0}),1.0]])]});}
            var Q17;
            {var subQ0=sQuery(id+"F8.wireOp",EDGE,"E90");var subQ1=makeQuery(id+"F1.opExtrude","CAP_EDGE",EDGE,{"disambiguationData":[OSD([sQuery(id+"F0.wireOp",EDGE,"E67")])],"isStart":false});var subQ2=makeQuery(id+"F8.imprint","INTERSECT",VERTEX,{"disambiguationData":[OD(0.0)],"derivedFrom":[subQ1,subQ0]});Q17=makeQuery(id+"F8.imprint","IMPRINT",FACE,{"disambiguationData":[TD([[makeQuery(id+"F8.imprint","IMPRINT",EDGE,{"disambiguationData":[TD([[subQ2,-1.0]])],"derivedFrom":subQ0}),1.0]])]});}
            var Q18;
            {var subQ0=sQuery(id+"F8.wireOp",EDGE,"E92");var subQ1=makeQuery(id+"F1.opExtrude","CAP_EDGE",EDGE,{"disambiguationData":[OSD([sQuery(id+"F0.wireOp",EDGE,"E13")])],"isStart":false});var subQ2=makeQuery(id+"F8.imprint","INTERSECT",VERTEX,{"disambiguationData":[OD(0.0)],"derivedFrom":[subQ1,subQ0]});Q18=makeQuery(id+"F8.imprint","IMPRINT",FACE,{"disambiguationData":[TD([[makeQuery(id+"F8.imprint","IMPRINT",EDGE,{"disambiguationData":[TD([[subQ2,1.0]])],"derivedFrom":subQ0}),1.0]])]});}
            var Q19;
            {var subQ0=sQuery(id+"F8.wireOp",EDGE,"E92");var subQ1=makeQuery(id+"F1.opExtrude","CAP_EDGE",EDGE,{"disambiguationData":[OSD([sQuery(id+"F0.wireOp",EDGE,"E13")])],"isStart":false});var subQ2=makeQuery(id+"F8.imprint","INTERSECT",VERTEX,{"disambiguationData":[OD(0.0)],"derivedFrom":[subQ1,subQ0]});Q19=makeQuery(id+"F8.imprint","IMPRINT",FACE,{"disambiguationData":[TD([[makeQuery(id+"F8.imprint","IMPRINT",EDGE,{"disambiguationData":[TD([[subQ2,-1.0]])],"derivedFrom":subQ0}),1.0]])]});}
            var Q20;
            {var subQ0=sQuery(id+"F8.wireOp",EDGE,"E92");var subQ1=makeQuery(id+"F1.opExtrude","CAP_EDGE",EDGE,{"disambiguationData":[OSD([sQuery(id+"F0.wireOp",EDGE,"E12")])],"isStart":false});var subQ2=makeQuery(id+"F8.imprint","INTERSECT",VERTEX,{"disambiguationData":[OD(0.0)],"derivedFrom":[subQ1,subQ0]});Q20=makeQuery(id+"F8.imprint","IMPRINT",FACE,{"disambiguationData":[TD([[makeQuery(id+"F8.imprint","IMPRINT",EDGE,{"disambiguationData":[TD([[subQ2,-1.0]])],"derivedFrom":subQ0}),1.0]])]});}
            var Q21;
            {var subQ0=sQuery(id+"F8.wireOp",EDGE,"E91");var subQ1=makeQuery(id+"F1.opExtrude","CAP_EDGE",EDGE,{"disambiguationData":[OSD([sQuery(id+"F0.wireOp",EDGE,"E13")])],"isStart":false});var subQ2=makeQuery(id+"F8.imprint","INTERSECT",VERTEX,{"disambiguationData":[OD(0.0)],"derivedFrom":[subQ1,subQ0]});Q21=makeQuery(id+"F8.imprint","IMPRINT",FACE,{"disambiguationData":[TD([[makeQuery(id+"F8.imprint","IMPRINT",EDGE,{"disambiguationData":[TD([[subQ2,1.0]])],"derivedFrom":subQ0}),1.0]])]});}
            var Q22;
            {var subQ0=sQuery(id+"F8.wireOp",EDGE,"E91");var subQ1=makeQuery(id+"F1.opExtrude","CAP_EDGE",EDGE,{"disambiguationData":[OSD([sQuery(id+"F0.wireOp",EDGE,"E13")])],"isStart":false});var subQ2=makeQuery(id+"F8.imprint","INTERSECT",VERTEX,{"disambiguationData":[OD(0.0)],"derivedFrom":[subQ1,subQ0]});Q22=makeQuery(id+"F8.imprint","IMPRINT",FACE,{"disambiguationData":[TD([[makeQuery(id+"F8.imprint","IMPRINT",EDGE,{"disambiguationData":[TD([[subQ2,-1.0]])],"derivedFrom":subQ0}),1.0]])]});}
            var Q23;
            {var subQ0=sQuery(id+"F8.wireOp",EDGE,"E91");var subQ1=makeQuery(id+"F1.opExtrude","CAP_EDGE",EDGE,{"disambiguationData":[OSD([sQuery(id+"F0.wireOp",EDGE,"E12")])],"isStart":false});var subQ2=makeQuery(id+"F8.imprint","INTERSECT",VERTEX,{"disambiguationData":[OD(0.0)],"derivedFrom":[subQ1,subQ0]});Q23=makeQuery(id+"F8.imprint","IMPRINT",FACE,{"disambiguationData":[TD([[makeQuery(id+"F8.imprint","IMPRINT",EDGE,{"disambiguationData":[TD([[subQ2,-1.0]])],"derivedFrom":subQ0}),1.0]])]});}
            var Q24;
            {var subQ0=sQuery(id+"F8.wireOp",EDGE,"E93");var subQ1=makeQuery(id+"F1.opExtrude","CAP_EDGE",EDGE,{"disambiguationData":[OSD([sQuery(id+"F0.wireOp",EDGE,"E13")])],"isStart":false});var subQ2=makeQuery(id+"F8.imprint","INTERSECT",VERTEX,{"disambiguationData":[OD(0.0)],"derivedFrom":[subQ1,subQ0]});Q24=makeQuery(id+"F8.imprint","IMPRINT",FACE,{"disambiguationData":[TD([[makeQuery(id+"F8.imprint","IMPRINT",EDGE,{"disambiguationData":[TD([[subQ2,1.0]])],"derivedFrom":subQ0}),1.0]])]});}
            var Q25;
            {var subQ0=sQuery(id+"F8.wireOp",EDGE,"E93");var subQ1=makeQuery(id+"F1.opExtrude","CAP_EDGE",EDGE,{"disambiguationData":[OSD([sQuery(id+"F0.wireOp",EDGE,"E13")])],"isStart":false});var subQ2=makeQuery(id+"F8.imprint","INTERSECT",VERTEX,{"disambiguationData":[OD(0.0)],"derivedFrom":[subQ1,subQ0]});Q25=makeQuery(id+"F8.imprint","IMPRINT",FACE,{"disambiguationData":[TD([[makeQuery(id+"F8.imprint","IMPRINT",EDGE,{"disambiguationData":[TD([[subQ2,-1.0]])],"derivedFrom":subQ0}),1.0]])]});}
            var Q26;
            {var subQ0=sQuery(id+"F8.wireOp",EDGE,"E93");var subQ1=makeQuery(id+"F1.opExtrude","CAP_EDGE",EDGE,{"disambiguationData":[OSD([sQuery(id+"F0.wireOp",EDGE,"E12")])],"isStart":false});var subQ2=makeQuery(id+"F8.imprint","INTERSECT",VERTEX,{"disambiguationData":[OD(0.0)],"derivedFrom":[subQ1,subQ0]});Q26=makeQuery(id+"F8.imprint","IMPRINT",FACE,{"disambiguationData":[TD([[makeQuery(id+"F8.imprint","IMPRINT",EDGE,{"disambiguationData":[TD([[subQ2,-1.0]])],"derivedFrom":subQ0}),1.0]])]});}
            var Q27;
            {var subQ0=sQuery(id+"F8.wireOp",EDGE,"E92");var subQ1=makeQuery(id+"F1.opExtrude","CAP_EDGE",EDGE,{"disambiguationData":[OSD([sQuery(id+"F0.wireOp",EDGE,"E12")])],"isStart":false});var subQ2=makeQuery(id+"F8.imprint","INTERSECT",VERTEX,{"disambiguationData":[OD(0.0)],"derivedFrom":[subQ1,subQ0]});Q27=makeQuery(id+"F8.imprint","IMPRINT",FACE,{"disambiguationData":[TD([[makeQuery(id+"F8.imprint","IMPRINT",EDGE,{"disambiguationData":[TD([[subQ2,1.0]])],"derivedFrom":subQ0}),1.0]])]});}
            var Q28;
            Q28=makeQuery(id+"F1.opExtrude","CAP_FACE",FACE,{"disambiguationData":[OSD([sQuery(id+"F0.wireOp",EDGE,"E0"),sQuery(id+"F0.wireOp",EDGE,"E1"),sQuery(id+"F0.wireOp",EDGE,"E2"),sQuery(id+"F0.wireOp",EDGE,"E3"),sQuery(id+"F0.wireOp",EDGE,"E4"),sQuery(id+"F0.wireOp",EDGE,"E5"),sQuery(id+"F0.wireOp",EDGE,"E6"),sQuery(id+"F0.wireOp",EDGE,"E7"),sQuery(id+"F0.wireOp",EDGE,"E8"),sQuery(id+"F0.wireOp",EDGE,"E9"),sQuery(id+"F0.wireOp",EDGE,"E10"),sQuery(id+"F0.wireOp",EDGE,"E11"),sQuery(id+"F0.wireOp",EDGE,"E12"),sQuery(id+"F0.wireOp",EDGE,"E13"),sQuery(id+"F0.wireOp",EDGE,"E14.filletArc"),sQuery(id+"F0.wireOp",EDGE,"E15.filletArc"),sQuery(id+"F0.wireOp",EDGE,"E16.filletArc"),sQuery(id+"F0.wireOp",EDGE,"E17.filletArc"),sQuery(id+"F0.wireOp",EDGE,"E18"),sQuery(id+"F0.wireOp",EDGE,"E19"),sQuery(id+"F0.wireOp",EDGE,"E20"),sQuery(id+"F0.wireOp",EDGE,"E21"),sQuery(id+"F0.wireOp",EDGE,"E22"),sQuery(id+"F0.wireOp",EDGE,"E23.filletArc"),sQuery(id+"F0.wireOp",EDGE,"E24.filletArc"),sQuery(id+"F0.wireOp",EDGE,"E25.filletArc"),sQuery(id+"F0.wireOp",EDGE,"E26.filletArc"),sQuery(id+"F0.wireOp",EDGE,"E27"),sQuery(id+"F0.wireOp",EDGE,"E28"),sQuery(id+"F0.wireOp",EDGE,"E29"),sQuery(id+"F0.wireOp",EDGE,"E30"),sQuery(id+"F0.wireOp",EDGE,"E31"),sQuery(id+"F0.wireOp",EDGE,"E32"),sQuery(id+"F0.wireOp",EDGE,"E33"),sQuery(id+"F0.wireOp",EDGE,"E34"),sQuery(id+"F0.wireOp",EDGE,"E35"),sQuery(id+"F0.wireOp",EDGE,"E36"),sQuery(id+"F0.wireOp",EDGE,"E37"),sQuery(id+"F0.wireOp",EDGE,"E38"),sQuery(id+"F0.wireOp",EDGE,"E39"),sQuery(id+"F0.wireOp",EDGE,"E40.filletArc"),sQuery(id+"F0.wireOp",EDGE,"E41.filletArc"),sQuery(id+"F0.wireOp",EDGE,"E42.filletArc"),sQuery(id+"F0.wireOp",EDGE,"E43.filletArc"),sQuery(id+"F0.wireOp",EDGE,"E44.filletArc"),sQuery(id+"F0.wireOp",EDGE,"E45.filletArc"),sQuery(id+"F0.wireOp",EDGE,"E46.filletArc"),sQuery(id+"F0.wireOp",EDGE,"E47"),sQuery(id+"F0.wireOp",EDGE,"E48"),sQuery(id+"F0.wireOp",EDGE,"E49"),sQuery(id+"F0.wireOp",EDGE,"E50"),sQuery(id+"F0.wireOp",EDGE,"E51"),sQuery(id+"F0.wireOp",EDGE,"E52"),sQuery(id+"F0.wireOp",EDGE,"E53"),sQuery(id+"F0.wireOp",EDGE,"E54.filletArc"),sQuery(id+"F0.wireOp",EDGE,"E55"),sQuery(id+"F0.wireOp",EDGE,"E56"),sQuery(id+"F0.wireOp",EDGE,"E57"),sQuery(id+"F0.wireOp",EDGE,"E58"),sQuery(id+"F0.wireOp",EDGE,"E59"),sQuery(id+"F0.wireOp",EDGE,"E60"),sQuery(id+"F0.wireOp",EDGE,"E61"),sQuery(id+"F0.wireOp",EDGE,"E62"),sQuery(id+"F0.wireOp",EDGE,"E63"),sQuery(id+"F0.wireOp",EDGE,"E64"),sQuery(id+"F0.wireOp",EDGE,"E65"),sQuery(id+"F0.wireOp",EDGE,"E66"),sQuery(id+"F0.wireOp",EDGE,"E67"),sQuery(id+"F0.wireOp",EDGE,"E68"),sQuery(id+"F0.wireOp",EDGE,"E69.filletArc"),sQuery(id+"F0.wireOp",EDGE,"E70.filletArc"),sQuery(id+"F0.wireOp",EDGE,"E71.filletArc"),sQuery(id+"F0.wireOp",EDGE,"E72.filletArc"),sQuery(id+"F0.wireOp",EDGE,"E73.filletArc"),sQuery(id+"F0.wireOp",EDGE,"E74.filletArc"),sQuery(id+"F0.wireOp",EDGE,"E75.filletArc"),sQuery(id+"F0.wireOp",EDGE,"E76.filletArc"),sQuery(id+"F0.wireOp",EDGE,"E77"),sQuery(id+"F0.wireOp",EDGE,"E78")])],"isStart":true});
            extrude(context, id + "F9", {"entities" : qUnion([Q0, Q1, Q2, Q3, Q4, Q5, Q6, Q7, Q8, Q9, Q10, Q11, Q12, Q13, Q14, Q15, Q16, Q17, Q18, Q19, Q20, Q21, Q22, Q23, Q24, Q25, Q26, Q27]), "operationType" : NewBodyOperationType.ADD, "endBound" : BoundingType.UP_TO_SURFACE, "oppositeDirection" : true, "endBoundEntityFace" : qUnion([Q28]), "depth" : 25.4 * mm});
        }
    });
